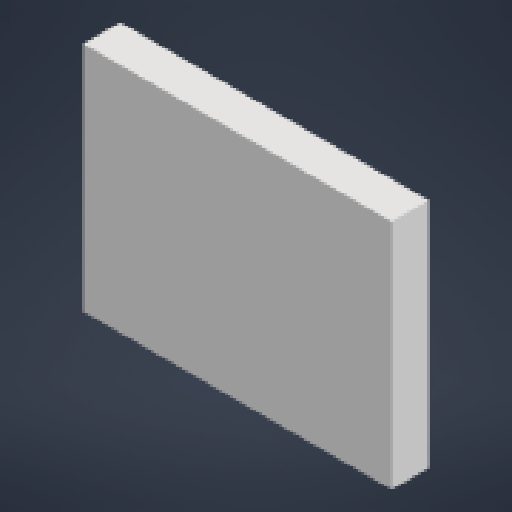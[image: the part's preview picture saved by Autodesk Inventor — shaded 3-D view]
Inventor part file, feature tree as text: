
AUTODESK INVENTOR PART (.ipt)
format: ipt  version: 2025.2 (Build 292293000, 293)  size: 115,712 bytes
history: native  units: in
note: dims shown in document units (in); Inventor stores cm internally (conversion verified against a paired STEP export)
features: reference x5, other x3, extrude x1, sketch x1
ambient origin geometry x8: Origin, YZ Plane, XZ Plane, XY Plane, X Axis, Y Axis, Z Axis, Center Point
bodies: Solid1 (feature_tree)
feature tree (10):
  extrude  "Extrusion1"  [1 undecoded]
  sketch  "Sketch1"  dims[d0=0.7874in d1=0.0in]
  reference  "Reference1"
  reference  "Reference2"
  reference  "Reference3"
  reference  "Reference4"
  reference  "Reference5"
  other  "18650ASSEMBLYfordrawing.iam"
  other  "PILLARSCELLCASE18650:1"
  other  "cooling plate:1"
note: 1 required parameter value undecoded (feature->parameter linkage not recoverable at this tier; creation-order binding heuristic only, values carry confidence <= 0.55)
